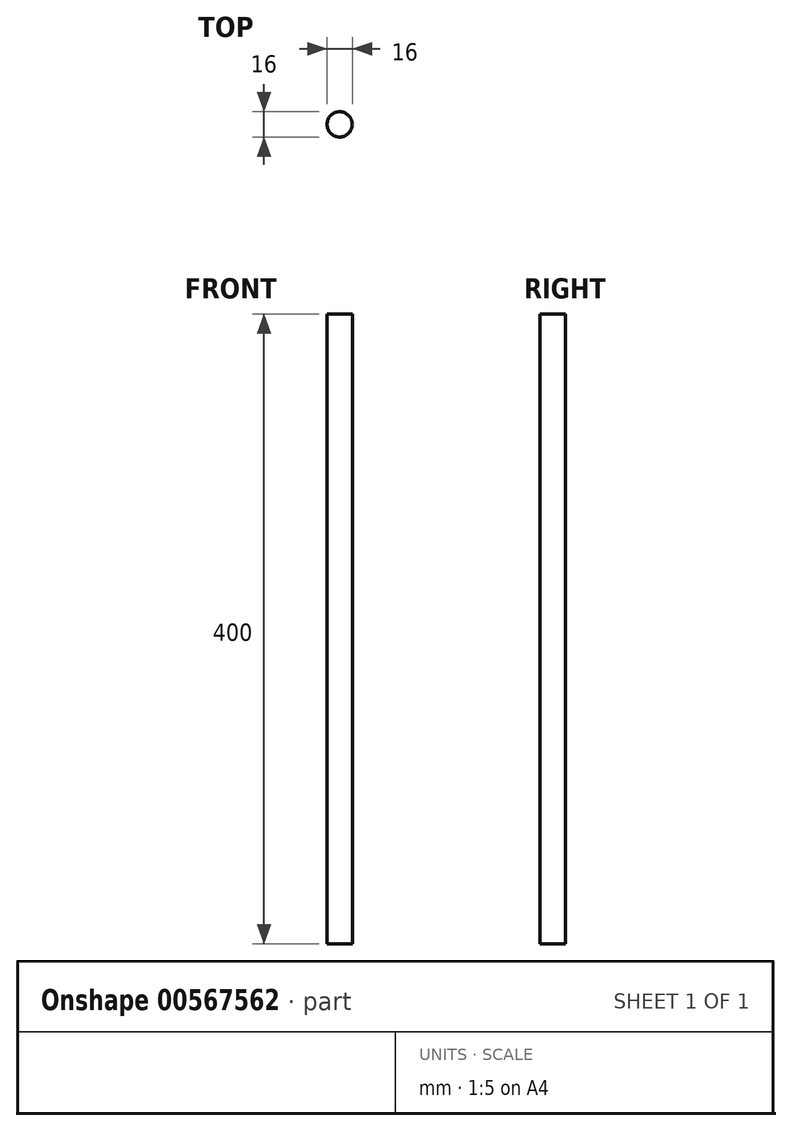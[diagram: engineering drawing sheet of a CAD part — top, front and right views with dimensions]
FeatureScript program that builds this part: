
annotation { "Feature Type Name" : "Feature", "Feature Type Description" : "" }
export const myFeature = defineFeature(function(context is Context, id is Id, definition is map)
    precondition{}
    {
        {
            var Q0;
            Q0=qCreatedBy(makeId("Top.planeOp"),FACE);
            var sketch = newSketch(context, id + "F0", { "sketchPlane" : qUnion([Q0])});
            skCircle(sketch, "E0", {"center": v(0, 0) * mm, "radius": 8 * mm});
            skSolve(sketch);
        }
        {
            var Q0;
            Q0=makeQuery(id+"F0.imprint","IMPRINT",FACE,{"disambiguationData":[TD([[makeQuery(id+"F0.imprint","IMPRINT",EDGE,{"derivedFrom":sQuery(id+"F0.wireOp",EDGE,"E0")}),1.0]])]});
            extrude(context, id + "F1", {"entities" : qUnion([Q0]), "depth" : 400 * mm, "offsetDistance" : 25 * mm});
        }
    });
